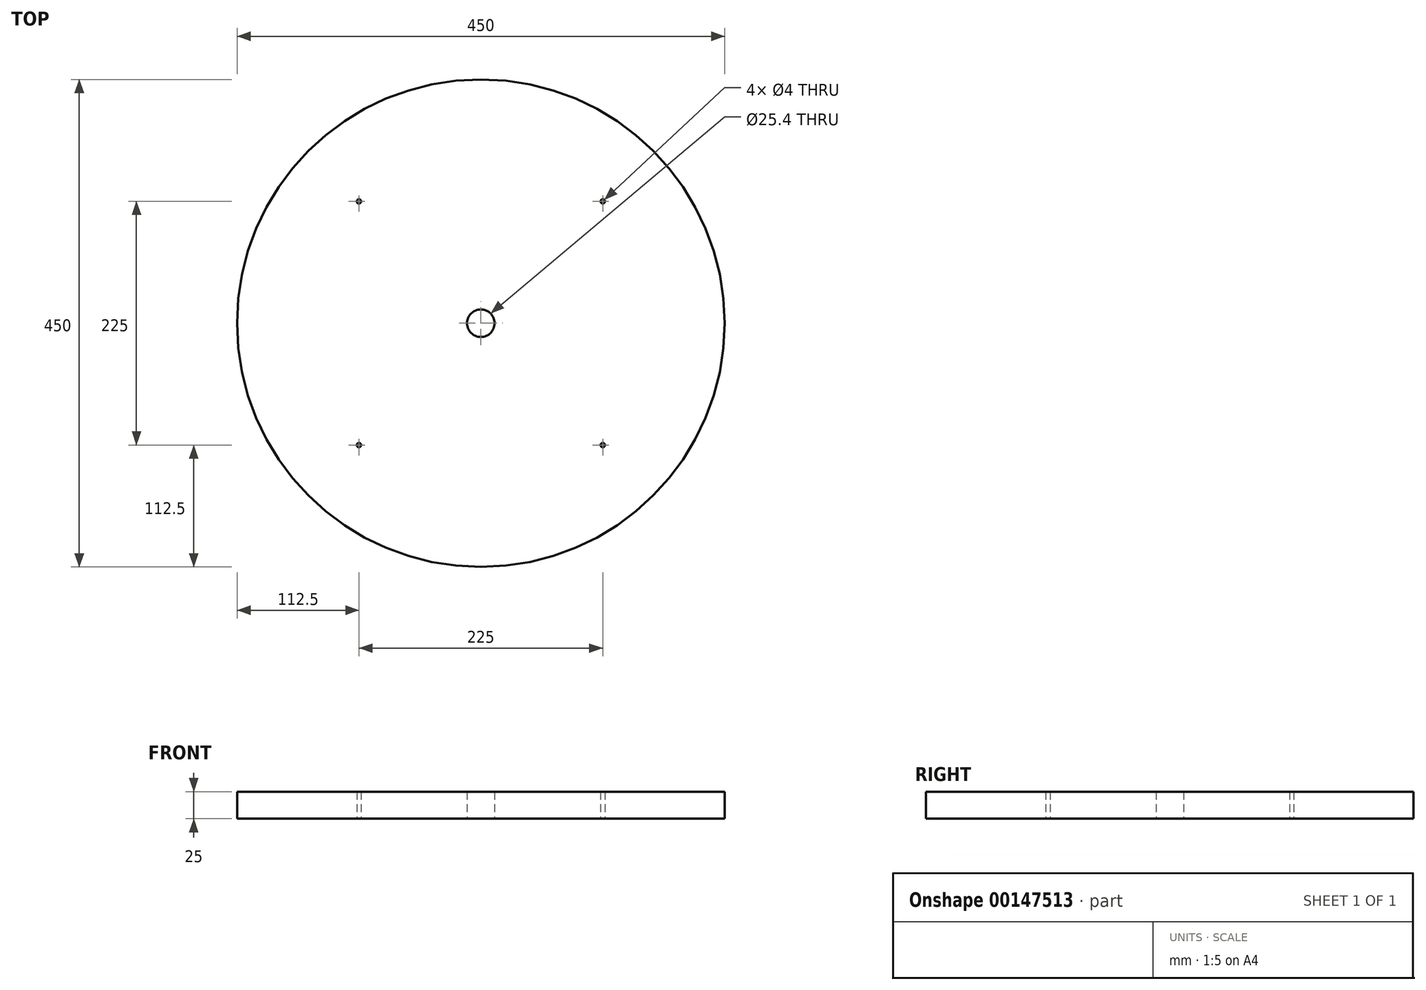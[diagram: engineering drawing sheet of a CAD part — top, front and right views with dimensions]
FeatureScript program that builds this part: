
annotation { "Feature Type Name" : "Feature", "Feature Type Description" : "" }
export const myFeature = defineFeature(function(context is Context, id is Id, definition is map)
    precondition{}
    {
        {
            var Q0;
            Q0=qCreatedBy(makeId("Top.planeOp"),FACE);
            var sketch = newSketch(context, id + "F0", { "sketchPlane" : qUnion([Q0])});
            skCircle(sketch, "E0", {"center": v(0, 0) * mm, "radius": 225 * mm});
            skCircle(sketch, "E1", {"center": v(0, 0) * mm, "radius": 12.7 * mm});
            skCircle(sketch, "E2", {"center": v(-112.5, 112.5) * mm, "radius": 2 * mm});
            skCircle(sketch, "E3.MirrorC", {"center": v(-112.5, -112.5) * mm, "radius": 2 * mm});
            skCircle(sketch, "E4.MirrorC", {"center": v(112.5, -112.5) * mm, "radius": 2 * mm});
            skCircle(sketch, "E5.MirrorC", {"center": v(112.5, 112.5) * mm, "radius": 2 * mm});
            skSolve(sketch);
        }
        {
            var Q0;
            Q0=makeQuery(id+"F0.imprint","IMPRINT",FACE,{"disambiguationData":[TD([[makeQuery(id+"F0.imprint","IMPRINT",EDGE,{"derivedFrom":sQuery(id+"F0.wireOp",EDGE,"E0")}),1.0]])]});
            extrude(context, id + "F1", {"entities" : qUnion([Q0]), "depth" : 25 * mm});
        }
    });
